# Revit family: CMD-503_Central de detección de CO
name_source: partatom
category: Equipos eléctricos
revit_build: Autodesk Revit 2017 (Build: 20190508_0315(x64)
units: mm (PartAtom-declared; Revit-internal decimal feet)

## family parameters
Anfitrión = Cara
Compartido = No
Corte con vacíos al cargar = No
Cota de conector redondo = Diámetro de uso
Punto de cálculo de habitación = No
Tipo de pieza = Otro panel

## types (1)
- CMD-503
    Altura = 443 mm
    Anchura = 268 mm
    Carga eléctrica = Otro
    Certificación = UNE 23300:1984
    Comentarios de tipo = Cada módulo de zona permite la conexión de hasta 32 detectores Detnov DMD-500 o DMDP-500. La conexión de
los detectores al módulo es a través de 2 hilos. Los detectores pueden ser distribuidos a lo largo de 2.000 metros de
longitud y cada detector cubre los 200 m² de superficie que define como máximo la normativa actual.
    Conexionado de la zona = 2 hilos
    Conexionado del módulo = Regleta extraíble Ø2,5mm²
    Código de montaje = PDETCMD-503
    Descripción = Central de detección de monóxido de carbono de 3 zonas. Marca Detnov, modelo CMD-503. Capacidad de hasta 32 detectores por módulo. Instalación a 2 hilos sin polaridad, distancia máxima de 2 Km. Dispone de 3 relés de nivel programables (extracción 1, extracción 2 y alarma). Los relés pueden configurarse para su activación con una avería. Dispone de dos formas de activación: estándar (por valor de cada detector) o por la medía real de toda la zona. Dispone de modo test para el mantenimiento de la instalación. Opcional: tarjeta TRMD-500 o TRMD-501 permite el control de un regulador de velocidad conectado a un motor consiguiendo eficiencia energética y reducción de ruido y vibraciones. Carcasa de plástico ABS, con posibilidad de ser empotrada. Dimensiones 439 x 268 x 112 mm. Alimentación a 230 Vac. Posibilidad de conexión de 2 baterías BTD-1207 (no incluidas). Certificado UNE 23300:1984.
    Distancia máxima de la zona = 2 km con cable de 1,5 mm²
    Elevación por defecto = 1219 mm
    Escala de medición = De 0 a 300 ppm de CO
    Fabricante = Detnov Security
    Fases = 1
    Humedad relativa = 95% sin condensación
    Imagen de tipo = <Ninguno>
    Modelo = Central CMD-503
    Modos de funcionamiento = Automático por máximos o promedio / ON / OFF
    Niveles de alarma = Programable de 0 a 299 ppm
    Niveles de extracción = Programable de 0 a 299 ppm
    Número máximo de detectores por zona = 32 detectores
    Número máximo de módulos de zona = De 1 a 3 zonas
    Peso (sin baterías) = 1.90 kg
    Potencia total = 0 VA
    Presentación de concentración = En ppm, 3 dígitos
    Profundidad = 112 mm
    Salidas de alarma = Relé (C, NC, NA)
    Salidas de extracción nivel 1 = Relé (C, NC, NA)
    Salidas de extracción nivel 2 = Relé (C, NC, NA)
    Teléfono = (+34) 93 371 60 25
    Temperatura trabajo = De -5ºC a 40ºC
    Tensión de alimentación = 90-264V / AC / 45W
    URL = https://www.detnov.com
    Voltaje_x = 230 V
    Índice IP = IP30
